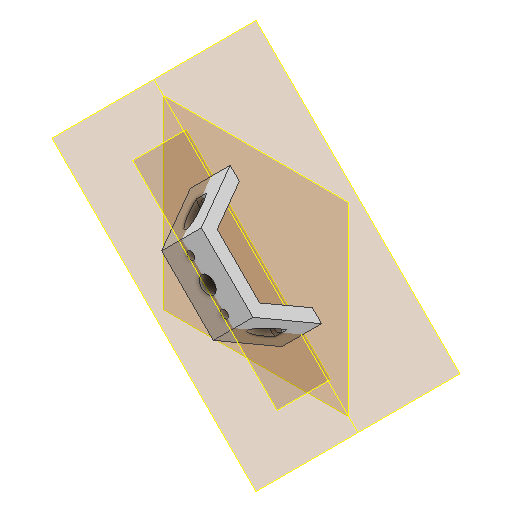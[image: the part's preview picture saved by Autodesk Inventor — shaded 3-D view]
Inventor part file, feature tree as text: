
AUTODESK INVENTOR PART (.ipt)
format: ipt  version: 2022 (Build 260153000, 153)  size: 161,280 bytes
history: native  units: in
note: dims shown in document units (in); Inventor stores cm internally (conversion verified against a paired STEP export)
features: reference x8, other x6, plane x4, sketch x3, extrude x2, hole x1, projected_geometry x1
ambient origin geometry x8: Origin, YZ Plane, XZ Plane, XY Plane, X Axis, Y Axis, Z Axis, Center Point
bodies: Solid1 (feature_tree)
feature tree (25):
  plane  "Work Plane1"
  other  "Work Axis1"
  plane  "Work Plane2"
  plane  "Work Plane3"
  extrude  "Extrusion1"  Depth=0.7874in
  hole  "Hole1"  [1 undecoded]
  extrude  "Extrusion2"  Depth=0.1575in
  plane  "Arbeitsebene4"
  sketch  "Sketch2"  dims[d0=90.0deg d1=0.7874in]
  sketch  "Sketch3"  dims[d2=60.0deg d3=120.0deg]
  sketch  "Sketch4"  dims[d5=0.1575in d6=0.1575in d7=0.1575in d8=0.7874in d9=0.0in d10=0.1102in d11=0.75in d12=0.2559in d13=0.4724in d14=0.5635in d15=1.0in d16=0.8108in d17=0.1102in d18=0.1102in d19=0.7874in d20=0.0in d24=0.2756in d25=0.2756in d26=0.5in d27=0.0344in]
  reference  "Reference6"
  projected_geometry  "Projected Loop1"
  reference  "Reference7"
  reference  "Reference8"
  reference  "Referenz11"
  reference  "Referenz12"
  reference  "Referenz13"
  reference  "Referenz18"
  reference  "Referenz19"
  other  "Anglerfish_bonne_mamman_v0.iam"
  other  "00_toslink_launcher_v3:3"
  other  "Anglerfish_bonne_mamman_m12large_v0.iam"
  other  "00_bonne_maman_jar:1"
  other  "Anglerfish_Lightplate_Tosslink:1"
note: 1 required parameter value undecoded (feature->parameter linkage not recoverable at this tier; creation-order binding heuristic only, values carry confidence <= 0.55)
